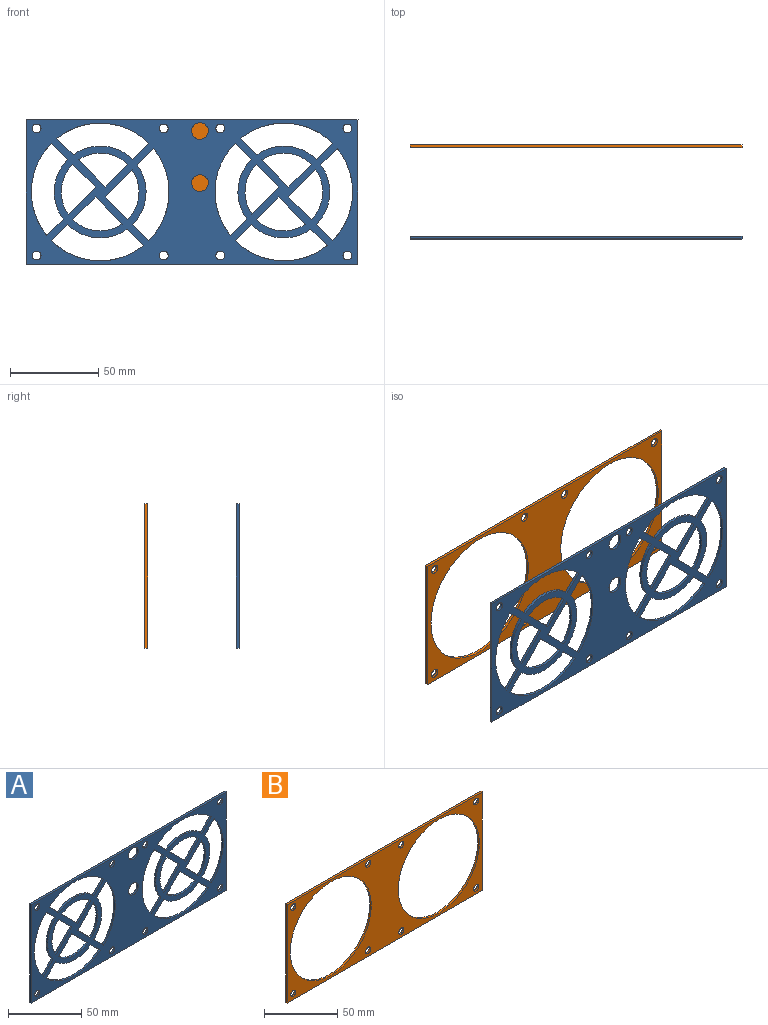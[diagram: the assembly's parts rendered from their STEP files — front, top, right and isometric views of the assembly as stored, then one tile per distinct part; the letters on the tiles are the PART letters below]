
ASSEMBLY  parts=2 mates=1
PART A: 72 faces, bbox 188x1.5x82 mm
  f0: cylinder r=22mm len=28.03mm, axis (0,1,0), area 45.8mm2, adj f1,f67,f68,f69
  f1: plane 12.73x12.73mm, normal (0.71,0,-0.71), area 27mm2, adj f0,f67,f68,f69
  f2: cylinder r=22mm len=28.03mm, axis (0,1,0), area 45.8mm2, adj f3,f43,f68,f69
  f3: plane 12.73x12.73mm, normal (-0.71,0,-0.71), area 27mm2, adj f2,f43,f68,f69
  f4: plane 15.3x15.3mm, normal (0.71,0,-0.71), area 32.4mm2, adj f5,f44,f68,f69
  f5: cylinder r=22mm len=28.03mm, axis (0,1,0), area 45.8mm2, adj f4,f44,f68,f69
  f6: cylinder r=22mm len=28.03mm, axis (0,1,0), area 45.8mm2, adj f7,f45,f68,f69
  f7: plane 12.73x12.73mm, normal (-0.71,0,0.71), area 27mm2, adj f6,f45,f68,f69
  f8: cylinder r=22mm len=28.03mm, axis (0,1,0), area 45.8mm2, adj f9,f46,f68,f69
  f9: plane 12.73x12.73mm, normal (0.71,0,0.71), area 27mm2, adj f8,f46,f68,f69
  f10: cylinder r=22mm len=28.03mm, axis (0,1,0), area 45.8mm2, adj f11,f47,f68,f69
  f11: plane 12.73x12.73mm, normal (0.71,0,-0.71), area 27mm2, adj f10,f47,f68,f69
  f12: cylinder r=22mm len=28.03mm, axis (0,1,0), area 45.8mm2, adj f13,f48,f68,f69
  f13: plane 12.73x12.73mm, normal (-0.71,0,-0.71), area 27mm2, adj f12,f48,f68,f69
  f14: plane 15.3x15.3mm, normal (0.71,0,0.71), area 32.4mm2, adj f15,f49,f68,f69
  f15: cylinder r=22mm len=28.03mm, axis (0,1,0), area 45.8mm2, adj f14,f49,f68,f69
  f16: plane 188x1.5mm, normal (0,0,1), area 282mm2, adj f17,f50,f68,f69
  f17: plane 82x1.5mm, normal (-1,0,0), area 123mm2, adj f16,f18,f68,f69
  f18: plane 188x1.5mm, normal (0,0,-1), area 282mm2, adj f17,f50,f68,f69
  f19: plane 9.27x9.27mm, normal (0.71,0,-0.71), area 19.7mm2, adj f20,f55,f68,f69
  f20: cylinder r=39mm len=52.18mm, axis (0,1,0), area 85.9mm2, adj f19,f21,f68,f69
  f21: plane 9.19x9.19mm, normal (0.71,0,0.71), area 19.5mm2, adj f20,f55,f68,f69
  f22: plane 9.27x9.27mm, normal (0.71,0,-0.71), area 19.7mm2, adj f23,f56,f68,f69
  f23: cylinder r=39mm len=52.18mm, axis (0,1,0), area 85.9mm2, adj f22,f24,f68,f69
  f24: plane 9.19x9.19mm, normal (0.71,0,0.71), area 19.5mm2, adj f23,f56,f68,f69
  f25: cylinder r=39mm len=52.18mm, axis (0,1,0), area 85.9mm2, adj f26,f61,f68,f69
  f26: plane 9.19x9.19mm, normal (-0.71,0,0.71), area 19.5mm2, adj f25,f27,f68,f69
  f27: cylinder r=26mm len=33.72mm, axis (0,1,0), area 55.2mm2, adj f26,f61,f68,f69
  f28: cylinder r=39mm len=52.18mm, axis (0,1,0), area 85.9mm2, adj f29,f62,f68,f69
  f29: plane 9.19x9.19mm, normal (-0.71,0,-0.71), area 19.5mm2, adj f28,f30,f68,f69
  f30: cylinder r=26mm len=33.72mm, axis (0,1,0), area 55.2mm2, adj f29,f62,f68,f69
  f31: cylinder r=39mm len=52.18mm, axis (0,1,0), area 85.9mm2, adj f32,f63,f68,f69
  f32: plane 9.19x9.19mm, normal (0.71,0,-0.71), area 19.5mm2, adj f31,f33,f68,f69
  f33: cylinder r=26mm len=33.72mm, axis (0,1,0), area 55.2mm2, adj f32,f63,f68,f69
  f34: cylinder r=39mm len=52.18mm, axis (0,1,0), area 85.9mm2, adj f35,f64,f68,f69
  f35: plane 9.19x9.19mm, normal (-0.71,0,0.71), area 19.5mm2, adj f34,f36,f68,f69
  f36: cylinder r=26mm len=33.72mm, axis (0,1,0), area 55.2mm2, adj f35,f64,f68,f69
  f37: cylinder r=39mm len=52.18mm, axis (0,1,0), area 85.9mm2, adj f38,f65,f68,f69
  f38: plane 9.19x9.19mm, normal (-0.71,0,-0.71), area 19.5mm2, adj f37,f39,f68,f69
  f39: cylinder r=26mm len=33.72mm, axis (0,1,0), area 55.2mm2, adj f38,f65,f68,f69
  f40: cylinder r=39mm len=52.18mm, axis (0,1,0), area 85.9mm2, adj f41,f66,f68,f69
  f41: plane 9.19x9.19mm, normal (0.71,0,-0.71), area 19.5mm2, adj f40,f42,f68,f69
  f42: cylinder r=26mm len=33.72mm, axis (0,1,0), area 55.2mm2, adj f41,f66,f68,f69
  f43: plane 15.3x15.3mm, normal (-0.71,0,0.71), area 32.4mm2, adj f2,f3,f68,f69
  f44: plane 12.73x12.73mm, normal (0.71,0,0.71), area 27mm2, adj f4,f5,f68,f69
  f45: plane 15.3x15.3mm, normal (0.71,0,0.71), area 32.4mm2, adj f6,f7,f68,f69
  f46: plane 15.3x15.3mm, normal (0.71,0,-0.71), area 32.4mm2, adj f8,f9,f68,f69
  f47: plane 15.3x15.3mm, normal (-0.71,0,-0.71), area 32.4mm2, adj f10,f11,f68,f69
  f48: plane 15.3x15.3mm, normal (-0.71,0,0.71), area 32.4mm2, adj f12,f13,f68,f69
  f49: plane 12.73x12.73mm, normal (-0.71,0,0.71), area 27mm2, adj f14,f15,f68,f69
  f50: plane 82x1.5mm, normal (1,0,0), area 123mm2, adj f16,f18,f68,f69
  f51: cylinder r=2.5mm len=5mm, axis (0,1,0), area 23.6mm2, adj f68,f69
  f52: cylinder r=2.5mm len=5mm, axis (0,1,0), area 23.6mm2, adj f68,f69
  f53: cylinder r=2.5mm len=5mm, axis (0,1,0), area 23.6mm2, adj f68,f69
  f54: cylinder r=2.5mm len=5mm, axis (0,1,0), area 23.6mm2, adj f68,f69
  f55: cylinder r=26mm len=33.72mm, axis (0,1,0), area 55.2mm2, adj f19,f21,f68,f69
  f56: cylinder r=26mm len=33.72mm, axis (0,1,0), area 55.2mm2, adj f22,f24,f68,f69
  f57: cylinder r=2.5mm len=5mm, axis (0,1,0), area 23.6mm2, adj f68,f69
  f58: cylinder r=2.5mm len=5mm, axis (0,1,0), area 23.6mm2, adj f68,f69
  f59: cylinder r=2.5mm len=5mm, axis (0,1,0), area 23.6mm2, adj f68,f69
  f60: cylinder r=2.5mm len=5mm, axis (0,1,0), area 23.6mm2, adj f68,f69
  f61: plane 9.27x9.27mm, normal (0.71,0,0.71), area 19.7mm2, adj f25,f27,f68,f69
  f62: plane 9.27x9.27mm, normal (-0.71,0,0.71), area 19.7mm2, adj f28,f30,f68,f69
  f63: plane 9.27x9.27mm, normal (-0.71,0,-0.71), area 19.7mm2, adj f31,f33,f68,f69
  f64: plane 9.27x9.27mm, normal (0.71,0,0.71), area 19.7mm2, adj f34,f36,f68,f69
  f65: plane 9.27x9.27mm, normal (-0.71,0,0.71), area 19.7mm2, adj f37,f39,f68,f69
  f66: plane 9.27x9.27mm, normal (-0.71,0,-0.71), area 19.7mm2, adj f40,f42,f68,f69
  f67: plane 15.3x15.3mm, normal (-0.71,0,-0.71), area 32.4mm2, adj f0,f1,f68,f69
  f68: plane 188x82mm, normal (0,-1,0), area 7884mm2, adj f0,f1,f2,f3,f4,f5,f6,f7
  f69: plane 188x82mm, normal (0,1,0), area 7884mm2, adj f0,f1,f2,f3,f4,f5,f6,f7
  f70: cylinder r=4.75mm len=9.5mm, axis (0,-1,0), area 44.8mm2, adj f68,f69
  f71: cylinder r=4.75mm len=9.5mm, axis (0,-1,0), area 44.8mm2, adj f68,f69
PART B: 16 faces, bbox 188x1.5x82 mm
  f0: plane 188x1.5mm, normal (0,0,1), area 282mm2, adj f1,f13,f14,f15
  f1: plane 82x1.5mm, normal (-1,0,0), area 123mm2, adj f0,f2,f14,f15
  f2: plane 188x1.5mm, normal (0,0,-1), area 282mm2, adj f1,f13,f14,f15
  f3: cylinder r=2.5mm len=5mm, axis (0,1,0), area 23.6mm2, adj f14,f15
  f4: cylinder r=2.5mm len=5mm, axis (0,1,0), area 23.6mm2, adj f14,f15
  f5: cylinder r=2.5mm len=5mm, axis (0,1,0), area 23.6mm2, adj f14,f15
  f6: cylinder r=2.5mm len=5mm, axis (0,1,0), area 23.6mm2, adj f14,f15
  f7: cylinder r=39mm len=78mm, axis (0,1,0), area 367.6mm2, adj f14,f15
  f8: cylinder r=39mm len=78mm, axis (0,1,0), area 367.6mm2, adj f14,f15
  f9: cylinder r=2.5mm len=5mm, axis (0,1,0), area 23.6mm2, adj f14,f15
  f10: cylinder r=2.5mm len=5mm, axis (0,1,0), area 23.6mm2, adj f14,f15
  f11: cylinder r=2.5mm len=5mm, axis (0,1,0), area 23.6mm2, adj f14,f15
  f12: cylinder r=2.5mm len=5mm, axis (0,1,0), area 23.6mm2, adj f14,f15
  f13: plane 82x1.5mm, normal (1,0,0), area 123mm2, adj f0,f2,f14,f15
  f14: plane 188x82mm, normal (0,-1,0), area 5702.2mm2, adj f0,f1,f2,f3,f4,f5,f6,f7
  f15: plane 188x82mm, normal (0,1,0), area 5702.2mm2, adj f0,f1,f2,f3,f4,f5,f6,f7
PLACE A t=(-0.46,3.25,-0.06)mm fixed
PLACE B t=(-0.46,55.07,-0.06)mm
MATE slider B.f3 <-> A.f51  axis (0,1,0) through (-88.46,53.57,35.94)mm
